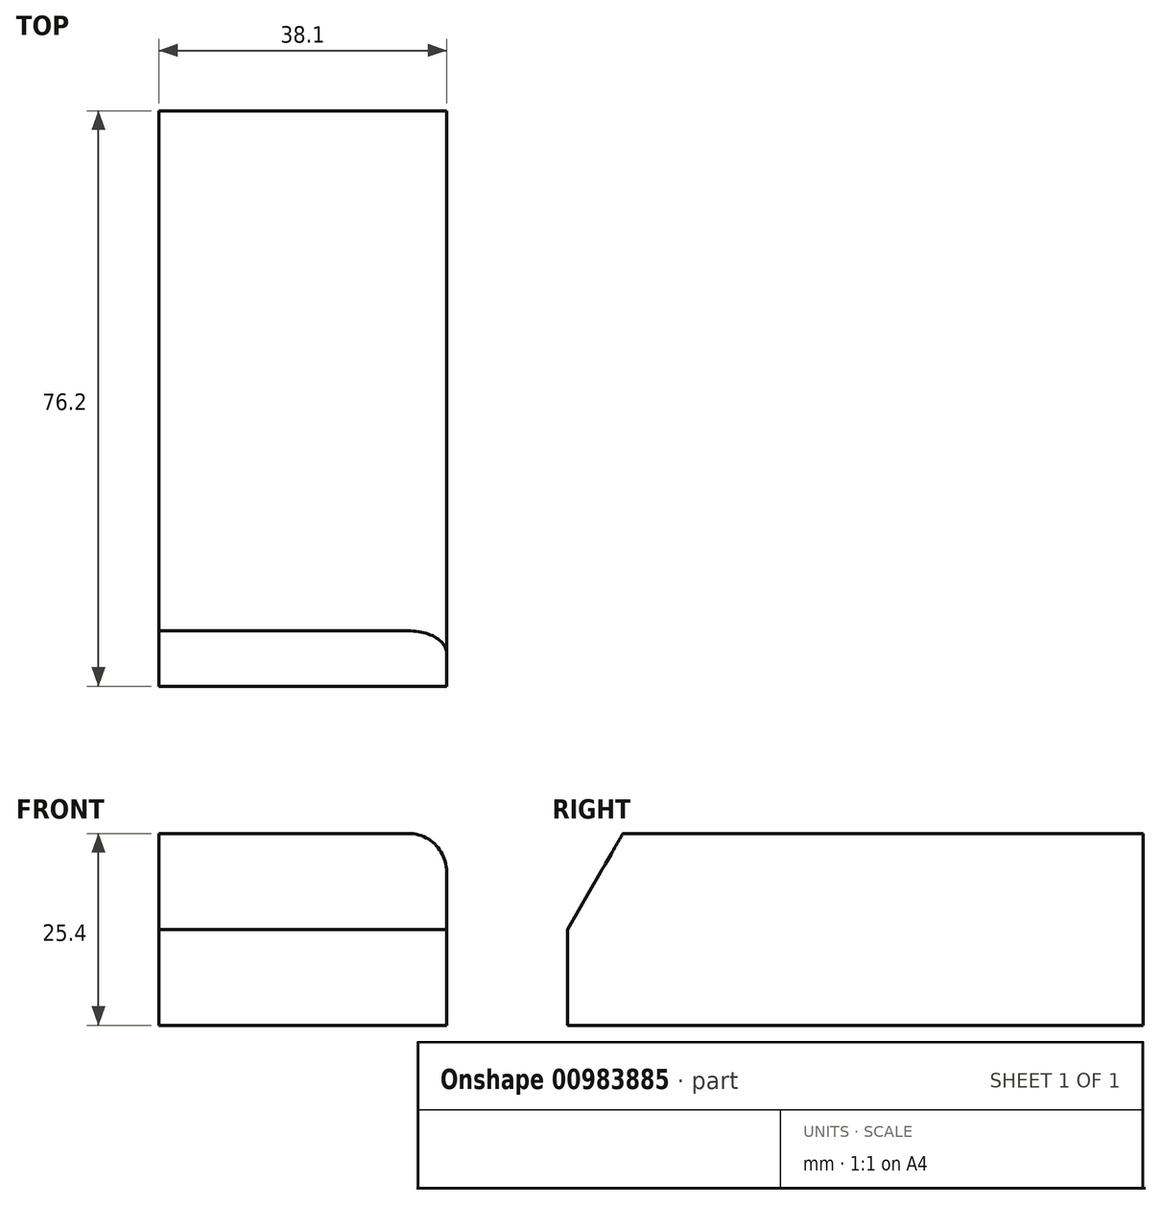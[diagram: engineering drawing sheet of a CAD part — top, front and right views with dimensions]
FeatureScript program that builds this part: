
annotation { "Feature Type Name" : "Feature", "Feature Type Description" : "" }
export const myFeature = defineFeature(function(context is Context, id is Id, definition is map)
    precondition{}
    {
        {
            var Q0;
            Q0=qCreatedBy(makeId("Top.planeOp"),FACE);
            var sketch = newSketch(context, id + "F0", { "sketchPlane" : qUnion([Q0])});
            skLineSegment(sketch, "E0.bottom", {"start": v(19.05, 38.1) * mm, "end": v(-19.05, 38.1) * mm});
            skLineSegment(sketch, "E0.top", {"start": v(19.05, -38.1) * mm, "end": v(-19.05, -38.1) * mm});
            skLineSegment(sketch, "E0.left", {"start": v(19.05, 38.1) * mm, "end": v(19.05, -38.1) * mm});
            skLineSegment(sketch, "E0.right", {"start": v(-19.05, 38.1) * mm, "end": v(-19.05, -38.1) * mm});
            skPoint(sketch, "E0.middle", {"position": v(0, 0) * mm});
            skSolve(sketch);
        }
        {
            var Q0;
            Q0=makeQuery(id+"F0.imprint","IMPRINT",FACE,{"disambiguationData":[TD([[makeQuery(id+"F0.imprint","IMPRINT",EDGE,{"derivedFrom":sQuery(id+"F0.wireOp",EDGE,"E0.bottom")}),1.0]])]});
            extrude(context, id + "F1", {"entities" : qUnion([Q0]), "depth" : 25.4 * mm, "offsetDistance" : 25.4 * mm});
        }
        {
            var Q0;
            Q0=makeQuery(id+"F1.opExtrude","CAP_EDGE",EDGE,{"disambiguationData":[OSD([sQuery(id+"F0.wireOp",EDGE,"E0.left")])],"isStart":false});
            fillet(context, id + "F2", {"entities" : qUnion([Q0]), "radius" : 5.08 * mm, "tangentPropagation" : true, "allowEdgeOverflow" : false});
        }
        {
            var Q0;
            Q0=makeQuery(id+"F1.opExtrude","CAP_EDGE",EDGE,{"disambiguationData":[OSD([sQuery(id+"F0.wireOp",EDGE,"E0.top")])],"isStart":false});
            chamfer(context, id + "F3", {"entities" : qUnion([Q0]), "chamferType" : ChamferType.OFFSET_ANGLE, "width" : 12.7 * mm, "oppositeDirection" : false, "angle" : 30 * degree});
        }
    });
